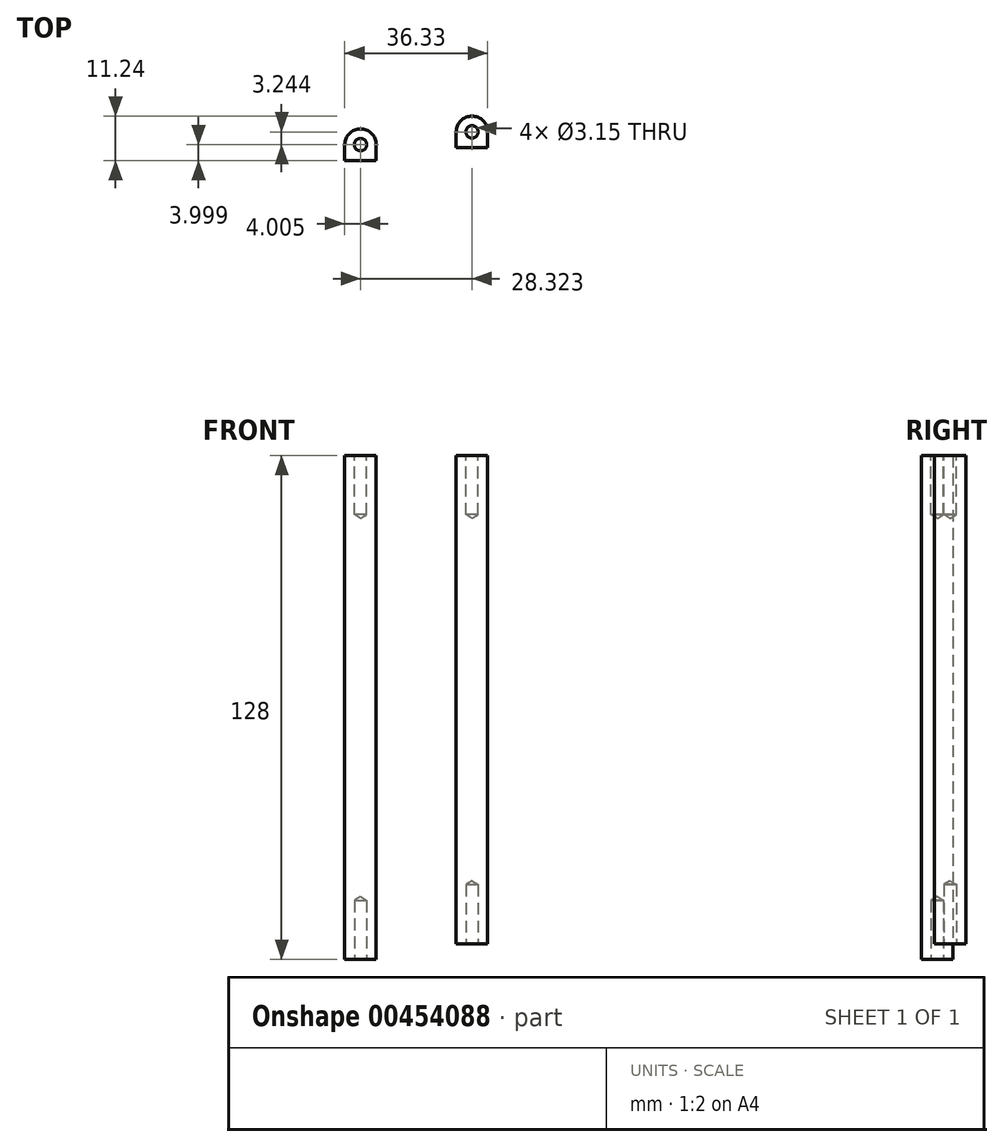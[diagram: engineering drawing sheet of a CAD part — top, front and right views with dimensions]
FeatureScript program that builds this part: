
annotation { "Feature Type Name" : "Feature", "Feature Type Description" : "" }
export const myFeature = defineFeature(function(context is Context, id is Id, definition is map)
    precondition{}
    {
        {
            var Q0;
            Q0=qCreatedBy(makeId("Top.planeOp"),FACE);
            var sketch = newSketch(context, id + "F0", { "sketchPlane" : qUnion([Q0])});
            skLineSegment(sketch, "E0.bottom", {"start": v(-3.72, -8.36) * mm, "end": v(4.28, -8.36) * mm});
            skLineSegment(sketch, "E0.top", {"start": v(-3.72, -16.36) * mm, "end": v(4.28, -16.36) * mm});
            skLineSegment(sketch, "E0.left", {"start": v(-3.72, -8.36) * mm, "end": v(-3.72, -16.36) * mm});
            skLineSegment(sketch, "E0.right", {"start": v(4.28, -8.36) * mm, "end": v(4.28, -16.36) * mm});
            skLineSegment(sketch, "E1", {"start": v(-3.72, -8.36) * mm, "end": v(4.28, -16.36) * mm, "construction": true});
            skPoint(sketch, "E2", {"position": v(0.28, -12.36) * mm});
            skLineSegment(sketch, "E3.bottom", {"start": v(24.6, -5.12) * mm, "end": v(32.6, -5.12) * mm});
            skLineSegment(sketch, "E3.top", {"start": v(24.6, -13.12) * mm, "end": v(32.6, -13.12) * mm});
            skLineSegment(sketch, "E3.left", {"start": v(24.6, -5.12) * mm, "end": v(24.6, -13.12) * mm});
            skLineSegment(sketch, "E3.right", {"start": v(32.6, -5.12) * mm, "end": v(32.6, -13.12) * mm});
            skLineSegment(sketch, "E4", {"start": v(24.6, -5.12) * mm, "end": v(32.6, -13.12) * mm, "construction": true});
            skPoint(sketch, "E5", {"position": v(28.6, -9.12) * mm});
            skSolve(sketch);
        }
        {
            var Q0;
            Q0=makeQuery(id+"F0.imprint","IMPRINT",FACE,{"disambiguationData":[TD([[makeQuery(id+"F0.imprint","IMPRINT",EDGE,{"derivedFrom":sQuery(id+"F0.wireOp",EDGE,"E0.bottom")}),-1.0]])]});
            extrude(context, id + "F1", {"entities" : qUnion([Q0]), "oppositeDirection" : true, "depth" : 128 * mm});
        }
        {
            var Q0;
            Q0=makeQuery(id+"F0.imprint","IMPRINT",FACE,{"disambiguationData":[TD([[makeQuery(id+"F0.imprint","IMPRINT",EDGE,{"derivedFrom":sQuery(id+"F0.wireOp",EDGE,"E3.bottom")}),-1.0]])]});
            extrude(context, id + "F2", {"entities" : qUnion([Q0]), "oppositeDirection" : true, "depth" : 124 * mm});
        }
        {
            var Q0;
            Q0=makeQuery(id+"F1.opExtrude","CAP_FACE",FACE,{"disambiguationData":[OSD([sQuery(id+"F0.wireOp",EDGE,"E0.bottom"),sQuery(id+"F0.wireOp",EDGE,"E0.left"),sQuery(id+"F0.wireOp",EDGE,"E0.right"),sQuery(id+"F0.wireOp",EDGE,"ADr0P0j2-xm2L-Hod2-eD0u-GFEYjQ3mg1ae")])],"isStart":false});
            var sketch = newSketch(context, id + "F3", { "sketchPlane" : qUnion([Q0])});
            skPoint(sketch, "E6", {"position": v(0.28, 12.36) * mm});
            skSolve(sketch);
        }
        {
            var Q0;
            Q0=makeQuery(id+"F2.opExtrude","CAP_FACE",FACE,{"disambiguationData":[OSD([sQuery(id+"F0.wireOp",EDGE,"E3.bottom"),sQuery(id+"F0.wireOp",EDGE,"E3.top"),sQuery(id+"F0.wireOp",EDGE,"E3.left"),sQuery(id+"F0.wireOp",EDGE,"E3.right")])],"isStart":false});
            var sketch = newSketch(context, id + "F4", { "sketchPlane" : qUnion([Q0])});
            skPoint(sketch, "E7", {"position": v(28.6, 9.12) * mm});
            skSolve(sketch);
        }
        {
            var Q0;
            Q0=sQuery(id+"F0.wireOp",VERTEX,"E2");
            var Q1;
            Q1=sQuery(id+"F3.wireOp",VERTEX,"E6");
            var Q2;
            Q2=sQuery(id+"F0.wireOp",VERTEX,"E5");
            var Q3;
            Q3=sQuery(id+"F4.wireOp",VERTEX,"E7");
            var Q4;
            Q4=makeQuery(id+"F1.opExtrude","SWEPT_BODY",BODY,{"disambiguationData":[OSD([sQuery(id+"F0.wireOp",EDGE,"E0.bottom"),sQuery(id+"F0.wireOp",EDGE,"E0.left"),sQuery(id+"F0.wireOp",EDGE,"E0.right"),sQuery(id+"F0.wireOp",EDGE,"ADr0P0j2-xm2L-Hod2-eD0u-GFEYjQ3mg1ae")])]});
            var Q5;
            Q5=makeQuery(id+"F2.opExtrude","SWEPT_BODY",BODY,{"disambiguationData":[OSD([sQuery(id+"F0.wireOp",EDGE,"E3.bottom"),sQuery(id+"F0.wireOp",EDGE,"E3.top"),sQuery(id+"F0.wireOp",EDGE,"E3.left"),sQuery(id+"F0.wireOp",EDGE,"E3.right")])]});
            hole(context, id + "F5", {"style" : HoleStyle.SIMPLE, "endStyle" : HoleEndStyle.BLIND, "standardTappedOrClearance" : lookupTablePath({ "standard" : "ISO", "fit" : "Close", "size" : "M3", "type" : "Clearance" }), "standardBlindInLast" : lookupTablePath({ "fit" : "Close", "standard" : "ISO", "size" : "M3", "type" : "Clearance" }), "holeDiameter" : 3.15 * mm, "holeDepth" : 15 * mm, "isTappedThrough" : true, "tappedDepth" : 12 * mm, "tapClearance" : 3, "locations" : qUnion([Q0, Q1, Q2, Q3]), "scope" : qUnion([Q4, Q5])});
        }
        {
            var Q0;
            Q0=makeQuery(id+"F1.opExtrude","SWEPT_EDGE",EDGE,{"disambiguationData":[OSD([sQuery(id+"F0.wireOp",EDGE,"E0.bottom"),sQuery(id+"F0.wireOp",EDGE,"E0.left")])]});
            var Q1;
            Q1=makeQuery(id+"F1.opExtrude","SWEPT_EDGE",EDGE,{"disambiguationData":[OSD([sQuery(id+"F0.wireOp",EDGE,"E0.bottom"),sQuery(id+"F0.wireOp",EDGE,"E0.right")])]});
            var Q2;
            Q2=makeQuery(id+"F2.opExtrude","SWEPT_EDGE",EDGE,{"disambiguationData":[OSD([sQuery(id+"F0.wireOp",EDGE,"E3.bottom"),sQuery(id+"F0.wireOp",EDGE,"E3.left")])]});
            var Q3;
            Q3=makeQuery(id+"F2.opExtrude","SWEPT_EDGE",EDGE,{"disambiguationData":[OSD([sQuery(id+"F0.wireOp",EDGE,"E3.bottom"),sQuery(id+"F0.wireOp",EDGE,"E3.right")])]});
            fillet(context, id + "F6", {"entities" : qUnion([Q0, Q1, Q2, Q3]), "radius" : 4 * mm, "tangentPropagation" : true, "allowEdgeOverflow" : false});
        }
    });
